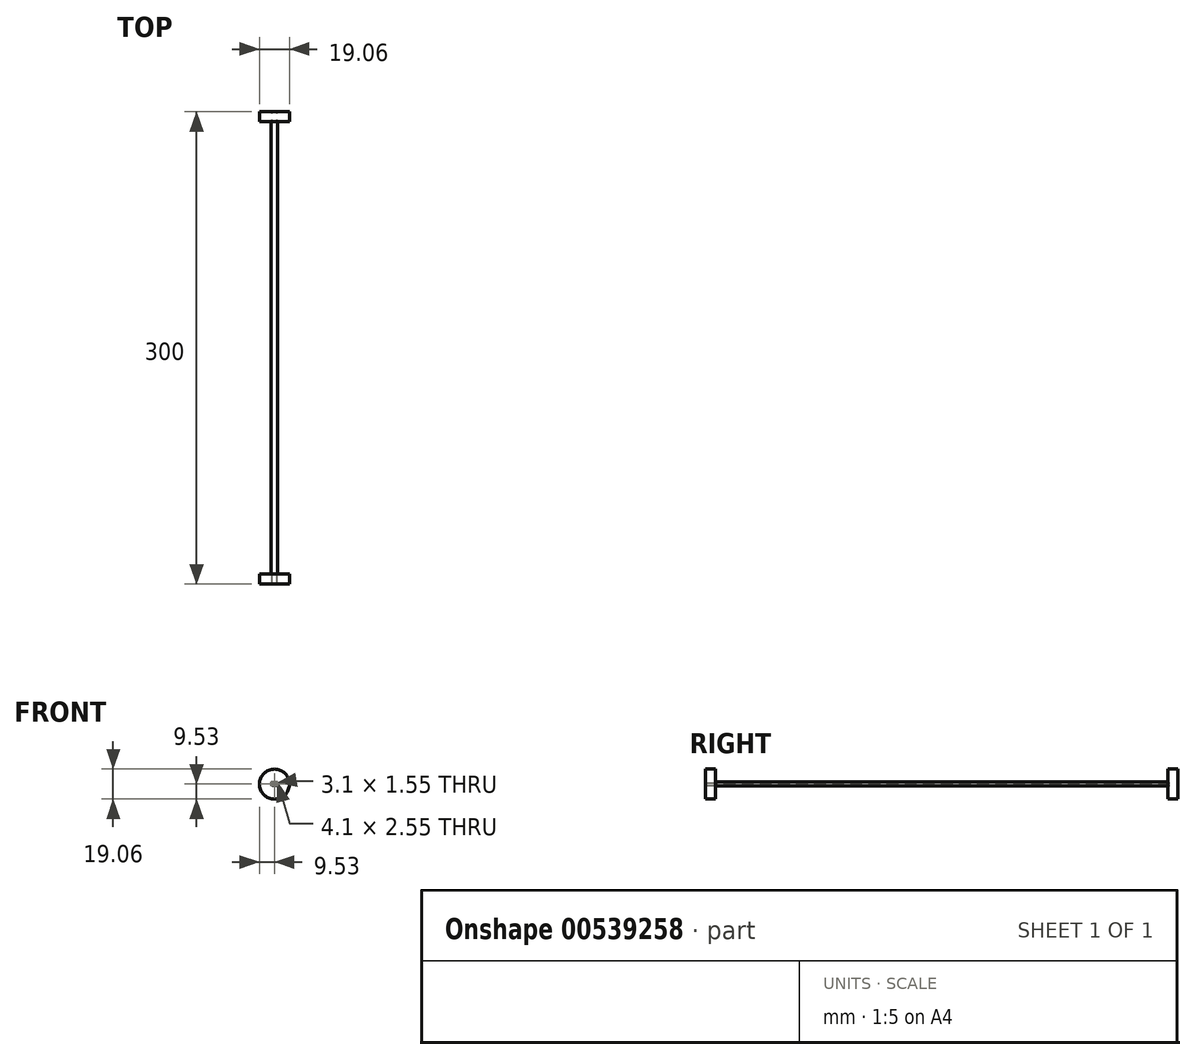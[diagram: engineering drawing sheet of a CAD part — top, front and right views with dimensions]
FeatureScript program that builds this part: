
annotation { "Feature Type Name" : "Feature", "Feature Type Description" : "" }
export const myFeature = defineFeature(function(context is Context, id is Id, definition is map)
    precondition{}
    {
        {
            var Q0;
            Q0=qCreatedBy(makeId("Front.planeOp"),FACE);
            var sketch = newSketch(context, id + "F0", { "sketchPlane" : qUnion([Q0])});
            skLineSegment(sketch, "E0.bottom", {"start": v(-1.55, -0.78) * mm, "end": v(1.55, -0.78) * mm});
            skLineSegment(sketch, "E0.top", {"start": v(-1.55, 0.78) * mm, "end": v(1.55, 0.78) * mm});
            skLineSegment(sketch, "E0.left", {"start": v(-1.55, -0.78) * mm, "end": v(-1.55, 0.78) * mm});
            skLineSegment(sketch, "E0.right", {"start": v(1.55, -0.78) * mm, "end": v(1.55, 0.78) * mm});
            skPoint(sketch, "E0.middle", {"position": v(0, 0) * mm});
            skLineSegment(sketch, "E1.bottom", {"start": v(2.05, -1.27) * mm, "end": v(-2.05, -1.28) * mm});
            skLineSegment(sketch, "E1.top", {"start": v(2.05, 1.28) * mm, "end": v(-2.05, 1.27) * mm});
            skLineSegment(sketch, "E1.left", {"start": v(2.05, -1.27) * mm, "end": v(2.05, 1.28) * mm});
            skLineSegment(sketch, "E1.right", {"start": v(-2.05, -1.28) * mm, "end": v(-2.05, 1.27) * mm});
            skSolve(sketch);
        }
        {
            assignVariable(context, id + "F1", {"name" : "cst_length", "anyValue" : 300});
        }
        {
            assignVariable(context, id + "F2", {"name" : "flange_thickness", "anyValue" : 6.35});
        }
        {
            var Q0;
            Q0=makeQuery(id+"F0.imprint","IMPRINT",FACE,{"disambiguationData":[TD([[makeQuery(id+"F0.imprint","IMPRINT",EDGE,{"derivedFrom":sQuery(id+"F0.wireOp",EDGE,"E0.bottom")}),-1.0]])]});
            extrude(context, id + "F3", {"entities" : qUnion([Q0]), "depth" : (getVariable(context, 'cst_length')) * mm, "offsetDistance" : 25 * mm});
        }
        {
            var Q0;
            Q0=makeQuery(id+"F3.opExtrude","CAP_FACE",FACE,{"disambiguationData":[OSD([sQuery(id+"F0.wireOp",EDGE,"E0.bottom"),sQuery(id+"F0.wireOp",EDGE,"E0.top"),sQuery(id+"F0.wireOp",EDGE,"E0.left"),sQuery(id+"F0.wireOp",EDGE,"E0.right"),sQuery(id+"F0.wireOp",EDGE,"E1.bottom"),sQuery(id+"F0.wireOp",EDGE,"E1.top"),sQuery(id+"F0.wireOp",EDGE,"E1.left"),sQuery(id+"F0.wireOp",EDGE,"E1.right")])],"isStart":false});
            var sketch = newSketch(context, id + "F4", { "sketchPlane" : qUnion([Q0])});
            skCircle(sketch, "E2", {"center": v(0, 0) * mm, "radius": 9.53 * mm});
            skSolve(sketch);
        }
        {
            var Q0;
            Q0=makeQuery(id+"F4.imprint","IMPRINT",FACE,{"disambiguationData":[TD([[makeQuery(id+"F4.imprint","IMPRINT",EDGE,{"derivedFrom":sQuery(id+"F4.wireOp",EDGE,"E2")}),1.0]])]});
            extrude(context, id + "F5", {"entities" : qUnion([Q0]), "operationType" : NewBodyOperationType.ADD, "oppositeDirection" : true, "depth" : (getVariable(context, 'flange_thickness')) * mm, "offsetDistance" : 25 * mm});
        }
        {
            var Q0;
            Q0=makeQuery(id+"F0.imprint","IMPRINT",FACE,{"disambiguationData":[TD([[makeQuery(id+"F0.imprint","IMPRINT",EDGE,{"derivedFrom":sQuery(id+"F0.wireOp",EDGE,"E0.bottom")}),-1.0]])]});
            var sketch = newSketch(context, id + "F6", { "sketchPlane" : qUnion([Q0])});
            skCircle(sketch, "E3", {"center": v(0, 0) * mm, "radius": 9.53 * mm});
            skSolve(sketch);
        }
        {
            var Q0;
            Q0=makeQuery(id+"F6.imprint","IMPRINT",FACE,{"disambiguationData":[TD([[makeQuery(id+"F6.imprint","IMPRINT",EDGE,{"derivedFrom":sQuery(id+"F6.wireOp",EDGE,"E3")}),1.0]])]});
            extrude(context, id + "F7", {"entities" : qUnion([Q0]), "operationType" : NewBodyOperationType.ADD, "depth" : (getVariable(context, 'flange_thickness')) * mm, "offsetDistance" : 25 * mm});
        }
    });
